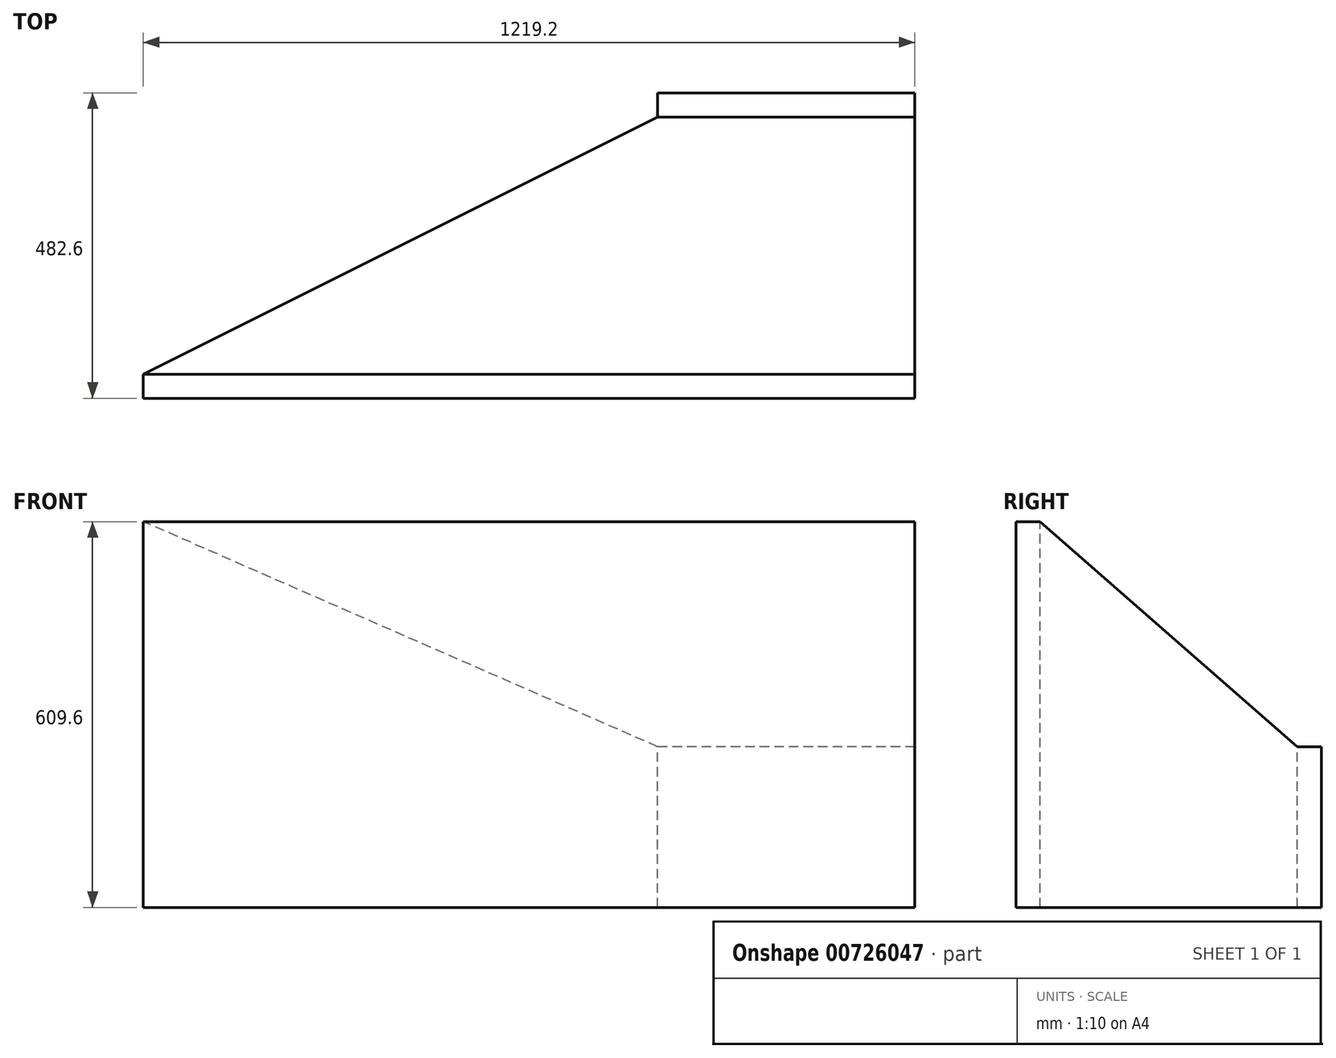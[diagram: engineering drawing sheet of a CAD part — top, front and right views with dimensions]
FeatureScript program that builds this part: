
annotation { "Feature Type Name" : "Feature", "Feature Type Description" : "" }
export const myFeature = defineFeature(function(context is Context, id is Id, definition is map)
    precondition{}
    {
        {
            var Q0;
            Q0=qCreatedBy(makeId("Front.planeOp"),FACE);
            var sketch = newSketch(context, id + "F0", { "sketchPlane" : qUnion([Q0])});
            skLineSegment(sketch, "E0.bottom", {"start": v(0, 0) * mm, "end": v(-406.4, 0) * mm});
            skLineSegment(sketch, "E0.top", {"start": v(0, 254) * mm, "end": v(-406.4, 254) * mm});
            skLineSegment(sketch, "E0.left", {"start": v(0, 0) * mm, "end": v(0, 254) * mm});
            skLineSegment(sketch, "E0.right", {"start": v(-406.4, 0) * mm, "end": v(-406.4, 254) * mm});
            skSolve(sketch);
        }
        {
            var Q0;
            Q0=qCreatedBy(makeId("Front.planeOp"),FACE);
            cPlane(context, id + "F1", {"entities" : qUnion([Q0]), "cplaneType" : CPlaneType.OFFSET, "offset" : 406.4 * mm, "width" : 152.4 * mm, "height" : 152.4 * mm});
        }
        {
            var Q0;
            Q0=qCreatedBy(id+"F1.planeOp",FACE);
            var sketch = newSketch(context, id + "F2", { "sketchPlane" : qUnion([Q0])});
            skLineSegment(sketch, "E1.bottom", {"start": v(0, 0) * mm, "end": v(-1219.2, 0) * mm});
            skLineSegment(sketch, "E1.top", {"start": v(0, 609.6) * mm, "end": v(-1219.2, 609.6) * mm});
            skLineSegment(sketch, "E1.left", {"start": v(0, 0) * mm, "end": v(0, 609.6) * mm});
            skLineSegment(sketch, "E1.right", {"start": v(-1219.2, 0) * mm, "end": v(-1219.2, 609.6) * mm});
            skSolve(sketch);
        }
        {
            var Q0;
            Q0=makeQuery(id+"F0.imprint","IMPRINT",FACE,{"disambiguationData":[TD([[makeQuery(id+"F0.imprint","IMPRINT",EDGE,{"derivedFrom":sQuery(id+"F0.wireOp",EDGE,"E0.bottom")}),-1.0]])]});
            var Q1;
            Q1=makeQuery(id+"F2.imprint","IMPRINT",FACE,{"disambiguationData":[TD([[makeQuery(id+"F2.imprint","IMPRINT",EDGE,{"derivedFrom":sQuery(id+"F2.wireOp",EDGE,"E1.bottom")}),-1.0]])]});
            loft(context, id + "F3", {"sheetProfilesArray" : [{ "sheetProfileEntities" : qUnion([Q0]) }, { "sheetProfileEntities" : qUnion([Q1]) }]});
        }
        {
            var Q0;
            Q0=makeQuery(id+"F3.opLoft","CAP_FACE",FACE,{"disambiguationData":[OSD([makeQuery(id+"F0.imprint","IMPRINT",FACE,{"disambiguationData":[TD([[makeQuery(id+"F0.imprint","IMPRINT",EDGE,{"derivedFrom":sQuery(id+"F0.wireOp",EDGE,"E0.bottom")}),-1.0]])]})])],"isStart":true});
            extrude(context, id + "F4", {"entities" : qUnion([Q0]), "operationType" : NewBodyOperationType.ADD, "depth" : 38.1 * mm, "offsetDistance" : 25.4 * mm});
        }
        {
            var Q0;
            Q0=makeQuery(id+"F3.opLoft","CAP_FACE",FACE,{"disambiguationData":[OSD([makeQuery(id+"F2.imprint","IMPRINT",FACE,{"disambiguationData":[TD([[makeQuery(id+"F2.imprint","IMPRINT",EDGE,{"derivedFrom":sQuery(id+"F2.wireOp",EDGE,"E1.bottom")}),-1.0]])]})])],"isStart":true});
            extrude(context, id + "F5", {"entities" : qUnion([Q0]), "operationType" : NewBodyOperationType.ADD, "depth" : 38.1 * mm, "offsetDistance" : 25.4 * mm});
        }
    });
